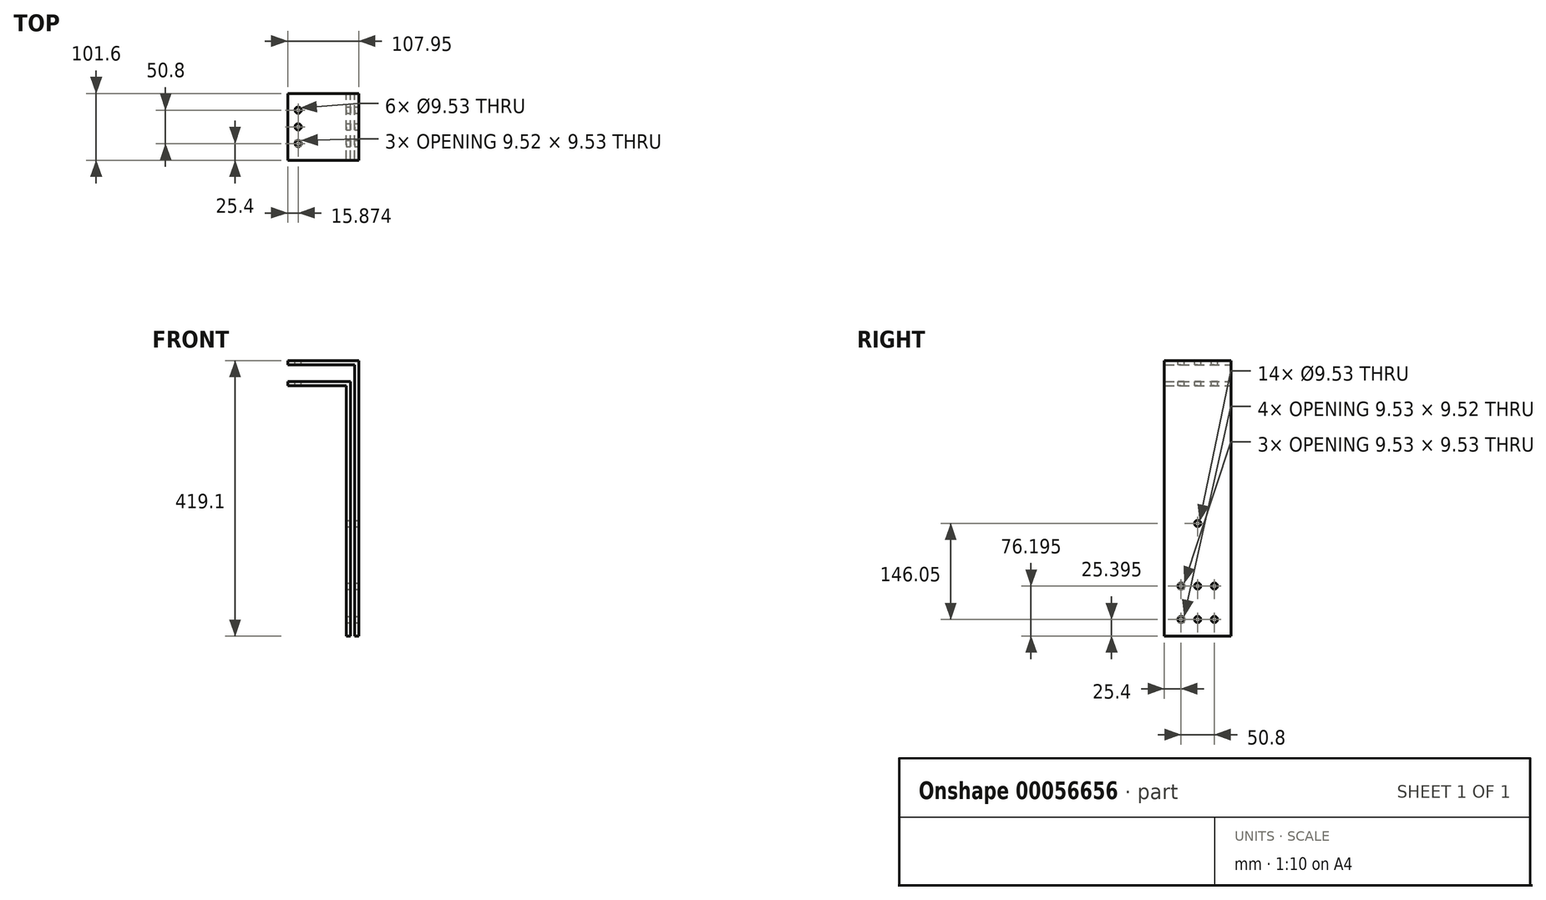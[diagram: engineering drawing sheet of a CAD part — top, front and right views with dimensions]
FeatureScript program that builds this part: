
annotation { "Feature Type Name" : "Feature", "Feature Type Description" : "" }
export const myFeature = defineFeature(function(context is Context, id is Id, definition is map)
    precondition{}
    {
        {
            var Q0;
            Q0=qCreatedBy(makeId("Front.planeOp"),FACE);
            var sketch = newSketch(context, id + "F0", { "sketchPlane" : qUnion([Q0])});
            skLineSegment(sketch, "E0", {"start": v(-138.97, 109.27) * mm, "end": v(-43.72, 109.27) * mm});
            skLineSegment(sketch, "E1", {"start": v(-43.72, 109.27) * mm, "end": v(-43.72, -278.08) * mm});
            skLineSegment(sketch, "E2", {"start": v(-50.07, 102.92) * mm, "end": v(-138.97, 102.92) * mm});
            skLineSegment(sketch, "E3", {"start": v(-37.37, 134.67) * mm, "end": v(-138.97, 134.67) * mm});
            skLineSegment(sketch, "E4", {"start": v(-138.97, 134.67) * mm, "end": v(-138.97, 141.02) * mm});
            skLineSegment(sketch, "E5", {"start": v(-138.97, 141.02) * mm, "end": v(-31.02, 141.02) * mm});
            skLineSegment(sketch, "E6", {"start": v(-31.02, 141.02) * mm, "end": v(-31.02, -278.08) * mm});
            skLineSegment(sketch, "E7", {"start": v(-50.07, -278.08) * mm, "end": v(-43.72, -278.08) * mm});
            skLineSegment(sketch, "E8.trimOffspring", {"start": v(-50.07, -278.08) * mm, "end": v(-50.07, 102.92) * mm});
            skLineSegment(sketch, "E9.trimOffspring", {"start": v(-37.37, -278.08) * mm, "end": v(-37.37, 134.67) * mm});
            skLineSegment(sketch, "E10.trimOffspring", {"start": v(-37.37, -278.08) * mm, "end": v(-31.02, -278.08) * mm});
            skLineSegment(sketch, "E11", {"start": v(-138.97, 109.27) * mm, "end": v(-138.97, 102.92) * mm});
            skSolve(sketch);
        }
        {
            var Q0;
            Q0=qSketchRegion(id+"F0",true);
            extrude(context, id + "F1", {"entities" : qUnion([Q0]), "endBound" : BoundingType.SYMMETRIC, "depth" : 101.6 * mm});
        }
        {
            var Q0;
            Q0=makeQuery(id+"F1.opExtrude","SWEPT_FACE",FACE,{"disambiguationData":[OSD([sQuery(id+"F0.wireOp",EDGE,"E6")])]});
            var sketch = newSketch(context, id + "F2", { "sketchPlane" : qUnion([Q0])});
            skCircle(sketch, "E12", {"center": v(-25.4, -252.68) * mm, "radius": 4.76 * mm});
            skCircle(sketch, "E13.0.1.0", {"center": v(-25.4, -201.88) * mm, "radius": 4.76 * mm});
            skCircle(sketch, "E13.1.0.0", {"center": v(0, -252.68) * mm, "radius": 4.76 * mm});
            skCircle(sketch, "E13.1.1.0", {"center": v(0, -201.88) * mm, "radius": 4.76 * mm});
            skCircle(sketch, "E13.2.0.0", {"center": v(25.4, -252.68) * mm, "radius": 4.76 * mm});
            skCircle(sketch, "E13.2.1.0", {"center": v(25.4, -201.88) * mm, "radius": 4.76 * mm});
            skLineSegment(sketch, "E13.direction1", {"start": v(-25.4, -252.68) * mm, "end": v(0, -252.68) * mm, "construction": true});
            skLineSegment(sketch, "E13.direction2", {"start": v(-25.4, -252.68) * mm, "end": v(-25.4, -201.88) * mm, "construction": true});
            skCircle(sketch, "E14", {"center": v(0, -106.63) * mm, "radius": 4.76 * mm});
            skSolve(sketch);
        }
        {
            var Q0;
            Q0=qSketchRegion(id+"F2",true);
            extrude(context, id + "F3", {"entities" : qUnion([Q0]), "operationType" : NewBodyOperationType.REMOVE, "endBound" : BoundingType.THROUGH_ALL, "oppositeDirection" : true, "depth" : 25.4 * mm});
        }
        {
            var Q0;
            Q0=makeQuery(id+"F1.opExtrude","SWEPT_FACE",FACE,{"disambiguationData":[OSD([sQuery(id+"F0.wireOp",EDGE,"E5")])]});
            var sketch = newSketch(context, id + "F4", { "sketchPlane" : qUnion([Q0])});
            skCircle(sketch, "E15", {"center": v(-123.1, -25.4) * mm, "radius": 4.76 * mm});
            skCircle(sketch, "E16.0.1.0", {"center": v(-123.1, 0) * mm, "radius": 4.76 * mm});
            skCircle(sketch, "E16.0.2.0", {"center": v(-123.1, 25.4) * mm, "radius": 4.76 * mm});
            skLineSegment(sketch, "E16.direction1", {"start": v(-123.1, -25.4) * mm, "end": v(-97.7, -25.4) * mm, "construction": true});
            skLineSegment(sketch, "E16.direction2", {"start": v(-123.1, -25.4) * mm, "end": v(-123.1, 0) * mm, "construction": true});
            skSolve(sketch);
        }
        {
            var Q0;
            Q0=qSketchRegion(id+"F4",true);
            extrude(context, id + "F5", {"entities" : qUnion([Q0]), "operationType" : NewBodyOperationType.REMOVE, "endBound" : BoundingType.THROUGH_ALL, "oppositeDirection" : true, "depth" : 25.4 * mm});
        }
    });
